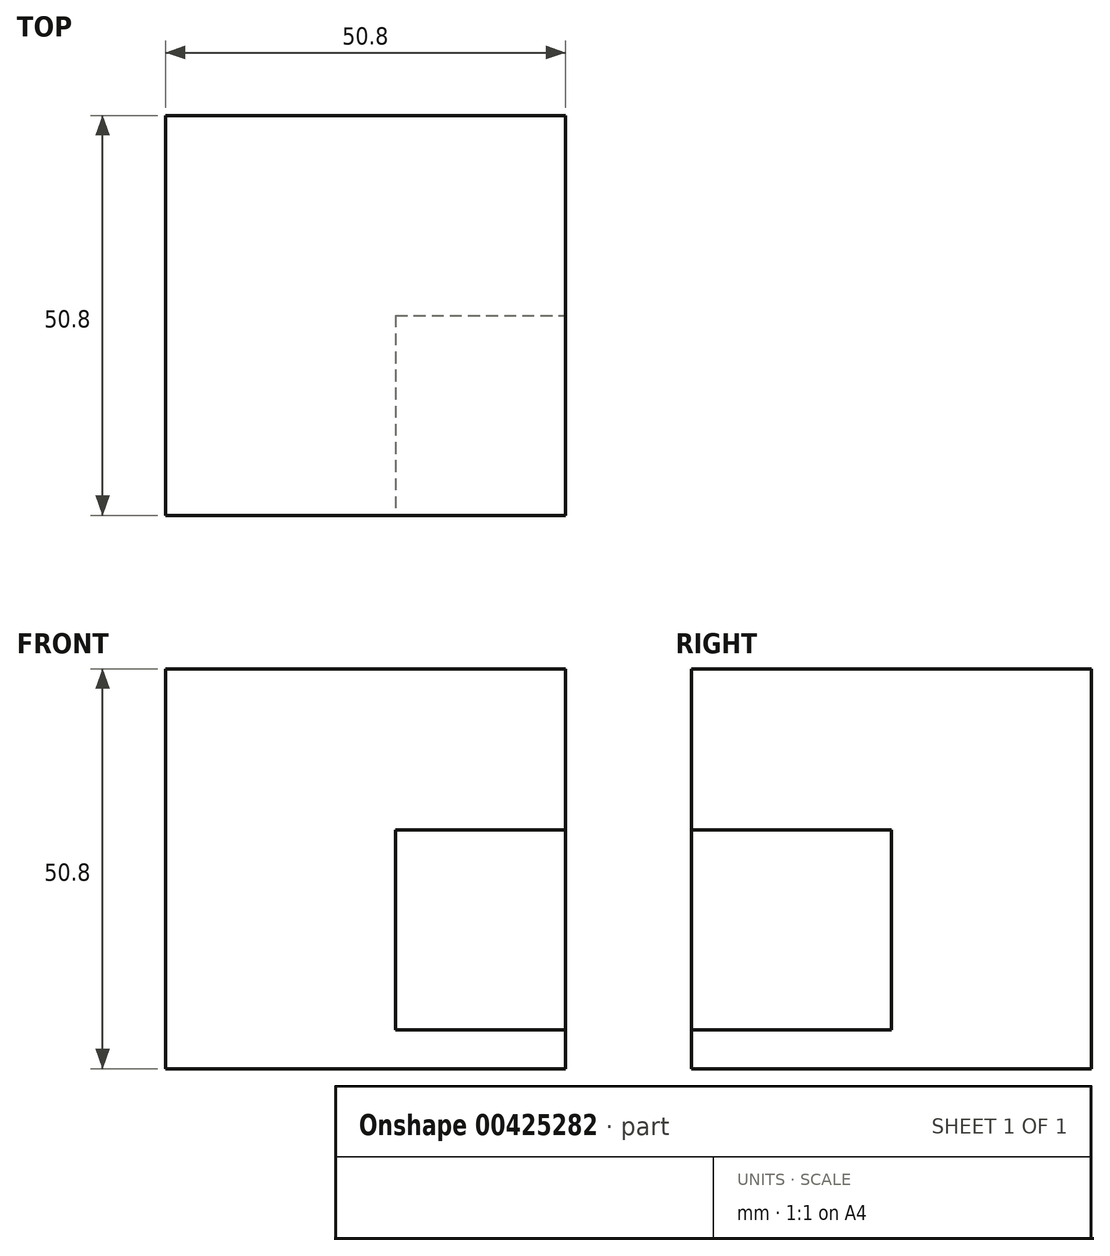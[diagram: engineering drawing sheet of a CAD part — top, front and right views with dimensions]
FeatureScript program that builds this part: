
annotation { "Feature Type Name" : "Feature", "Feature Type Description" : "" }
export const myFeature = defineFeature(function(context is Context, id is Id, definition is map)
    precondition{}
    {
        {
            var Q0;
            Q0=qCreatedBy(makeId("Front.planeOp"),FACE);
            var sketch = newSketch(context, id + "F0", { "sketchPlane" : qUnion([Q0])});
            skLineSegment(sketch, "E0", {"start": v(-46.97, 48.7) * mm, "end": v(-46.97, -2.1) * mm});
            skLineSegment(sketch, "E1", {"start": v(-46.97, -2.1) * mm, "end": v(3.83, -2.1) * mm});
            skLineSegment(sketch, "E2", {"start": v(3.83, -2.1) * mm, "end": v(3.83, 48.7) * mm});
            skLineSegment(sketch, "E3", {"start": v(3.83, 48.7) * mm, "end": v(-46.97, 48.7) * mm});
            skSolve(sketch);
        }
        {
            var Q0;
            Q0 = qSketchRegion(id + "F0", true);
            extrude(context, id + "F1", {"entities" : qUnion([Q0]), "depth" : 50.8 * mm});
        }
        {
            var Q0;
            Q0=makeQuery(id+"F1.opExtrude","CAP_FACE",FACE,{"disambiguationData":[OSD([sQuery(id+"F0.wireOp",EDGE,"E0"),sQuery(id+"F0.wireOp",EDGE,"E1"),sQuery(id+"F0.wireOp",EDGE,"E2"),sQuery(id+"F0.wireOp",EDGE,"E3")])],"isStart":false});
            var sketch = newSketch(context, id + "F2", { "sketchPlane" : qUnion([Q0])});
            skLineSegment(sketch, "E4", {"start": v(-17.75, 28.24) * mm, "end": v(-17.75, 2.84) * mm});
            skLineSegment(sketch, "E5", {"start": v(-17.75, 28.24) * mm, "end": v(7.65, 28.24) * mm});
            skLineSegment(sketch, "E6", {"start": v(7.65, 28.24) * mm, "end": v(7.65, 2.84) * mm});
            skLineSegment(sketch, "E7", {"start": v(-17.75, 2.84) * mm, "end": v(7.65, 2.84) * mm});
            skSolve(sketch);
        }
        {
            var Q0;
            {var subQ0=sQuery(id+"F2.wireOp",EDGE,"E4");Q0=makeQuery(id+"F2.imprint","IMPRINT",FACE,{"disambiguationData":[TD([[makeQuery(id+"F2.imprint","IMPRINT",EDGE,{"derivedFrom":subQ0}),1.0]])]});}
            extrude(context, id + "F3", {"entities" : qUnion([Q0]), "operationType" : NewBodyOperationType.REMOVE, "oppositeDirection" : true, "depth" : 25.4 * mm});
        }
    });
